# Revit family: РИДАН_Клапан поворотный HFE-3R (DN20-100)
name_source: partatom
category: Арматура трубопроводов
units: mm (PartAtom-declared; Revit-internal decimal feet)

## family parameters
Всегда вертикально = Да
На основе рабочей плоскости = Нет
Общий = Нет
При загрузке вырезать с полостями = Нет
Размер круглого соединителя = Использовать диаметр
Тип детали = Вставляется

## types (8) — shared parameters
ADSK_Версия Revit = 2019
ADSK_Версия семейства = 1.0
ADSK_Единица измерения = шт.
ADSK_Завод-изготовитель = ООО «Ридан-Трейд»
ADSK_Классификация нагрузок = Прочее
ADSK_Количество = 1
ADSK_Количество фаз = 1
ADSK_Коэффициент мощности = 1
ADSK_Потеря давления жидкости = 0.0 Па
ADSK_Расход жидкости = 0 м³/ч
DN150 = Нет
DN20_125 = Да
LT = HFE-3R
LT_EL = Electro
URL = https://ridan.ru
a = 2 мм
n2 = 58 мм
r = 115 мм
Изготовитель = ООО «Ридан-Трейд»
Привод_AMB162R_1 = ► : AMB-162R-Имп,60 c,24 AC,2-/3-поз.
Привод_AMB162R_2 = ► : AMB-162R-Имп,120 c,24 AC,2-/3-поз.
Привод_AMB162R_3 = ► : AMB-162R-Имп,60 c,230,2-/3-поз.
Привод_AMB162R_4 = ► : AMB-162R-Имп,120 c,230,2-/3-поз.
Привод_AMB162R_5 = ► : AMB-162R-Ан,60 или 120 c,24 AC/DC,0(2)–10 В
Привод_Рукоятка = ► : Рукоятка
Расход_А = 0 м³/ч
Расход_В = 0 м³/ч

## per-type parameters (varying)
- DN 20: ADSK_Диаметр условный=20 мм; ADSK_Код изделия=065Z0428R; ADSK_Марка=HFE-3R DN20; ADSK_Масса=4.1; ADSK_Наименование=Клапан регулирующий поворотный HFE-3R фланцевый PN6, Tmax=110C, DN20, Kvs=12 м3\ч; ADSK_Пропускная способность=12 м³/ч; b=12 мм; c=7 мм; d=49 мм; e=98 мм; f=73 мм; g=90 мм; h=51 мм; i=47 мм; j=42 мм; k=33 мм; l=56 мм; m=27 мм; n=39 мм; n1=39 мм; n3=38 мм; o=53 мм; p=12 мм; s=140 мм; s1=70 мм
- DN 25: ADSK_Диаметр условный=25 мм; ADSK_Код изделия=065Z0429R; ADSK_Марка=HFE-3R DN25; ADSK_Масса=4.6; ADSK_Наименование=Клапан регулирующий поворотный HFE-3R фланцевый PN6, Tmax=110C, DN25, Kvs=18 м3\ч; ADSK_Пропускная способность=18 м³/ч; b=12 мм; c=11 мм; d=50 мм; e=100 мм; f=73 мм; g=100 мм; h=64 мм; i=60 мм; j=51 мм; k=39 мм; l=56 мм; m=27 мм; n=39 мм; n1=39 мм; n3=38 мм; o=53 мм; p=12 мм; s=150 мм; s1=75 мм
- DN 32: ADSK_Диаметр условный=32 мм; ADSK_Код изделия=065Z0430R; ADSK_Марка=HFE-3R DN32; ADSK_Масса=6.8; ADSK_Наименование=Клапан регулирующий поворотный HFE-3R фланцевый PN6, Tmax=110C, DN32, Kvs=28 м3\ч; ADSK_Пропускная способность=28 м³/ч; b=14 мм; c=4 мм; d=60 мм; e=120 мм; f=104 мм; g=120 мм; h=71 мм; i=67 мм; j=62 мм; k=52 мм; l=64 мм; m=33 мм; n=45 мм; n1=45 мм; n3=44 мм; o=74 мм; p=15 мм; s=160 мм; s1=80 мм
- DN 40: ADSK_Диаметр условный=40 мм; ADSK_Код изделия=065Z0431R; ADSK_Марка=HFE-3R DN40; ADSK_Масса=7.6; ADSK_Наименование=Клапан регулирующий поворотный HFE-3R фланцевый PN6, Tmax=110C, DN40, Kvs=44 м3\ч; ADSK_Пропускная способность=44 м³/ч; b=13 мм; c=10 мм; d=63 мм; e=126 мм; f=103 мм; g=130 мм; h=86 мм; i=82 мм; j=68 мм; k=55 мм; l=64 мм; m=33 мм; n=45 мм; n1=45 мм; n3=44 мм; o=74 мм; p=15 мм; s=175 мм; s1=88 мм
- DN 50: ADSK_Диаметр условный=50 мм; ADSK_Код изделия=065Z0432R; ADSK_Марка=HFE-3R DN50; ADSK_Масса=9.6; ADSK_Наименование=Клапан регулирующий поворотный HFE-3R фланцевый PN6, Tmax=110C, DN50, Kvs=60 м3\ч; ADSK_Пропускная способность=60 м³/ч; b=13 мм; c=12 мм; d=70 мм; e=140 мм; f=125 мм; g=140 мм; h=96 мм; i=92 мм; j=78 мм; k=65 мм; l=81 мм; m=41 мм; n=53 мм; n1=53 мм; n3=52 мм; o=95 мм; p=15 мм; s=195 мм; s1=97 мм
- DN 65: ADSK_Диаметр условный=65 мм; ADSK_Код изделия=065Z0433R; ADSK_Марка=HFE-3R DN65; ADSK_Масса=11.8; ADSK_Наименование=Клапан регулирующий поворотный HFE-3R фланцевый PN6, Tmax=110C, DN65, Kvs=90 м3\ч; ADSK_Пропускная способность=90 м³/ч; b=14 мм; c=12 мм; d=72 мм; e=145 мм; f=125 мм; g=160 мм; h=116 мм; i=112 мм; j=97 мм; k=80 мм; l=86 мм; m=41 мм; n=53 мм; n1=53 мм; n3=52 мм; o=95 мм; p=15 мм; s=200 мм; s1=100 мм
- DN 80: ADSK_Диаметр условный=80 мм; ADSK_Код изделия=065Z0434R; ADSK_Марка=HFE-3R DN80; ADSK_Масса=17.2; ADSK_Наименование=Клапан регулирующий поворотный HFE-3R фланцевый PN6, Tmax=110C, DN80, Kvs=150 м3\ч; ADSK_Пропускная способность=150 м³/ч; b=17 мм; c=12 мм; d=87 мм; e=174 мм; f=148 мм; g=190 мм; h=120 мм; i=116 мм; j=97 мм; k=80 мм; l=109 мм; m=53 мм; n=65 мм; n1=65 мм; n3=64 мм; o=116 мм; p=15 мм; s=235 мм; s1=117 мм
- DN 100: ADSK_Диаметр условный=100 мм; ADSK_Код изделия=065Z0435R; ADSK_Марка=HFE-3R DN100; ADSK_Масса=23.7; ADSK_Наименование=Клапан регулирующий поворотный HFE-3R фланцевый PN6, Tmax=110C, DN100, Kvs=225 м3\ч; ADSK_Пропускная способность=225 м³/ч; b=16 мм; c=3 мм; d=112 мм; e=223 мм; f=170 мм; g=210 мм; h=140 мм; i=136 мм; j=126 мм; k=118 мм; l=127 мм; m=63 мм; n=75 мм; n1=75 мм; n3=74 мм; o=140 мм; p=15 мм; s=265 мм; s1=133 мм
